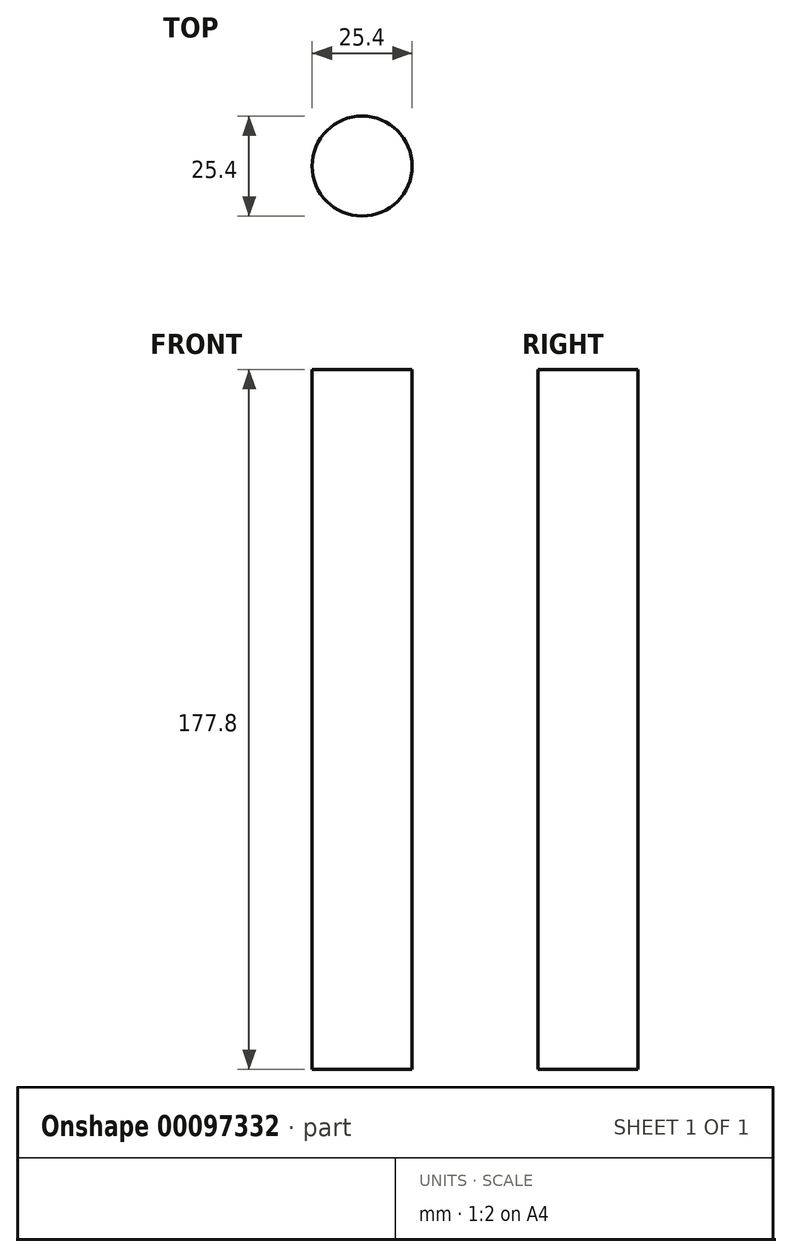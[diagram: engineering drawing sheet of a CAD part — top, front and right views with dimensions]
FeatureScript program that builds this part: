
annotation { "Feature Type Name" : "Feature", "Feature Type Description" : "" }
export const myFeature = defineFeature(function(context is Context, id is Id, definition is map)
    precondition{}
    {
        {
            var Q0;
            Q0=qCreatedBy(makeId("Top.planeOp"),FACE);
            var sketch = newSketch(context, id + "F0", { "sketchPlane" : qUnion([Q0])});
            skCircle(sketch, "E0", {"center": v(0, 0) * mm, "radius": 12.7 * mm});
            skSolve(sketch);
        }
        {
            var Q0;
            Q0=makeQuery(id+"F0.imprint","IMPRINT",FACE,{"disambiguationData":[TD([[makeQuery(id+"F0.imprint","IMPRINT",EDGE,{"derivedFrom":sQuery(id+"F0.wireOp",EDGE,"E0")}),1.0]])]});
            extrude(context, id + "F1", {"entities" : qUnion([Q0]), "depth" : 177.8 * mm});
        }
    });
